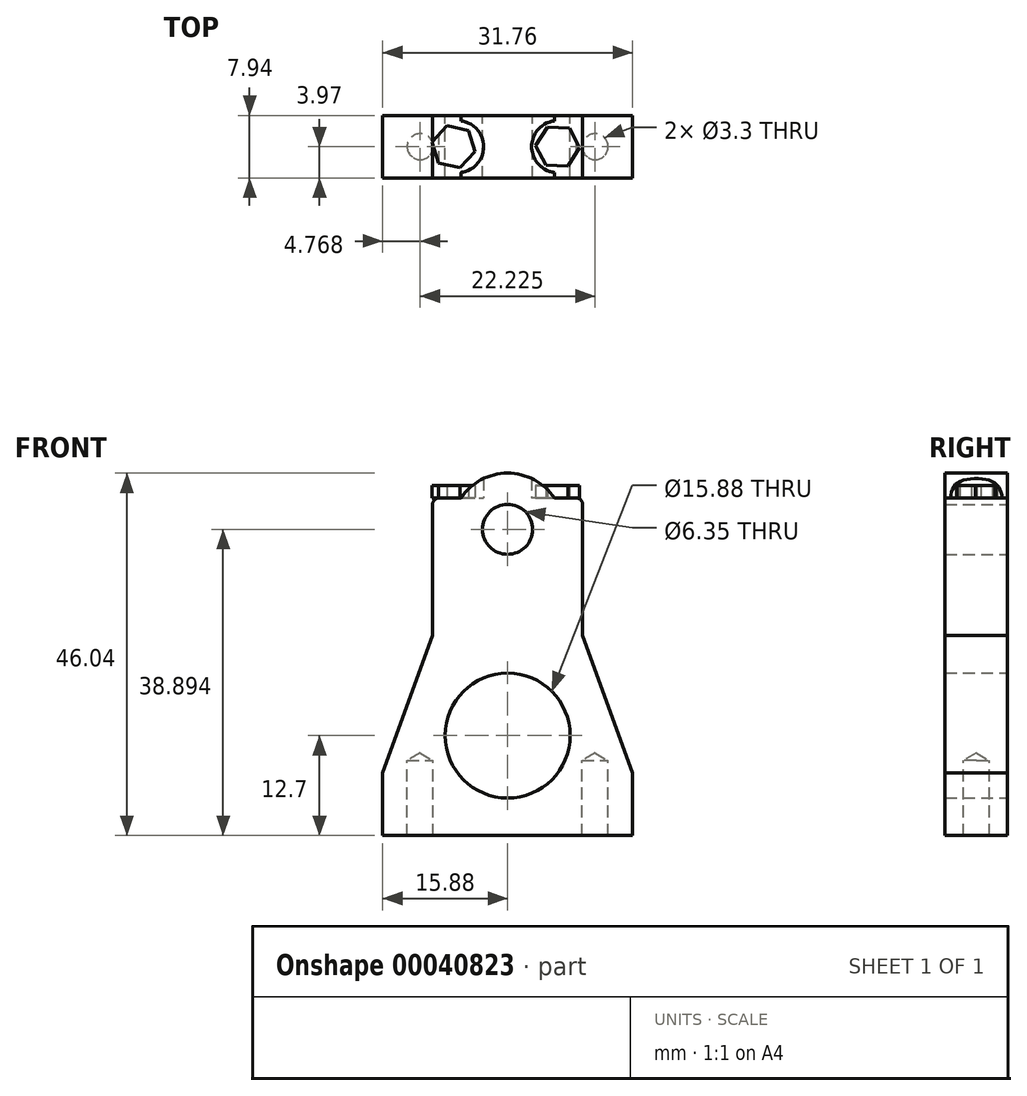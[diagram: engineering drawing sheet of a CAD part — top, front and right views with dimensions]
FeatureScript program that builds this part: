
annotation { "Feature Type Name" : "Feature", "Feature Type Description" : "" }
export const myFeature = defineFeature(function(context is Context, id is Id, definition is map)
    precondition{}
    {
        {
            var Q0;
            Q0=qCreatedBy(makeId("Front.planeOp"),FACE);
            var sketch = newSketch(context, id + "F0", { "sketchPlane" : qUnion([Q0])});
            skLineSegment(sketch, "E0.bottom", {"start": v(-15.88, 0) * mm, "end": v(15.88, 0) * mm});
            skLineSegment(sketch, "E0.top", {"start": v(-9.53, 42.86) * mm, "end": v(-5.94, 42.86) * mm});
            skLineSegment(sketch, "E0.left", {"start": v(-15.88, 0) * mm, "end": v(-15.88, 7.94) * mm});
            skLineSegment(sketch, "E0.right", {"start": v(15.88, 0) * mm, "end": v(15.87, 7.94) * mm});
            skCircle(sketch, "E1", {"center": v(0, 12.7) * mm, "radius": 7.94 * mm});
            skLineSegment(sketch, "E2", {"start": v(-9.53, 25.4) * mm, "end": v(-15.88, 7.94) * mm});
            skLineSegment(sketch, "E3", {"start": v(-9.53, 25.4) * mm, "end": v(-9.53, 42.86) * mm});
            skLineSegment(sketch, "E4", {"start": v(9.53, 42.86) * mm, "end": v(9.53, 25.4) * mm});
            skLineSegment(sketch, "E5", {"start": v(9.53, 25.4) * mm, "end": v(15.88, 7.94) * mm});
            skLineSegment(sketch, "E6", {"start": v(-9.53, 38.9) * mm, "end": v(9.53, 38.9) * mm, "construction": true});
            skArc(sketch, "E7", {"start": v(5.94, 42.86) * mm, "mid": v(0, 46.04) * mm, "end": v(-5.94, 42.86) * mm});
            skLineSegment(sketch, "E8.trimOffspring", {"start": v(5.94, 42.86) * mm, "end": v(9.53, 42.86) * mm});
            skCircle(sketch, "E9", {"center": v(0, 38.9) * mm, "radius": 3.18 * mm});
            skSolve(sketch);
        }
        {
            var Q0;
            Q0=qSketchRegion(id+"F0",true);
            extrude(context, id + "F1", {"entities" : qUnion([Q0]), "depth" : 7.94 * mm, "symmetric" : true});
        }
        {
            var Q0;
            Q0=makeQuery(id+"F1.opExtrude","SWEPT_EDGE",EDGE,{"disambiguationData":[OSD([sQuery(id+"F0.wireOp",EDGE,"E0.top"),sQuery(id+"F0.wireOp",EDGE,"E3")])]});
            var Q1;
            Q1=makeQuery(id+"F1.opExtrude","SWEPT_EDGE",EDGE,{"disambiguationData":[OSD([sQuery(id+"F0.wireOp",EDGE,"E4"),sQuery(id+"F0.wireOp",EDGE,"E8.trimOffspring")])]});
            fillet(context, id + "F2", {"entities" : qUnion([Q0, Q1]), "radius" : 0.8 * mm, "tangentPropagation" : true, "allowEdgeOverflow" : false});
        }
        {
            var Q0;
            Q0=makeQuery(id+"F1.opExtrude","SWEPT_FACE",FACE,{"disambiguationData":[OSD([sQuery(id+"F0.wireOp",EDGE,"E0.bottom")])]});
            var sketch = newSketch(context, id + "F3", { "sketchPlane" : qUnion([Q0])});
            skPoint(sketch, "E10", {"position": v(-11.11, 0) * mm});
            skPoint(sketch, "E11", {"position": v(11.11, 0) * mm});
            skSolve(sketch);
        }
        {
            var Q0;
            Q0=sQuery(id+"F3.wireOp",VERTEX,"E10");
            var Q1;
            Q1=sQuery(id+"F3.wireOp",VERTEX,"E11");
            var Q2;
            Q2=makeQuery(id+"F1.opExtrude","SWEPT_BODY",BODY,{"disambiguationData":[OSD([sQuery(id+"F0.wireOp",EDGE,"E0.bottom"),sQuery(id+"F0.wireOp",EDGE,"E0.top"),sQuery(id+"F0.wireOp",EDGE,"E0.left"),sQuery(id+"F0.wireOp",EDGE,"E0.right"),sQuery(id+"F0.wireOp",EDGE,"E1"),sQuery(id+"F0.wireOp",EDGE,"E2"),sQuery(id+"F0.wireOp",EDGE,"E3"),sQuery(id+"F0.wireOp",EDGE,"E4"),sQuery(id+"F0.wireOp",EDGE,"E5"),sQuery(id+"F0.wireOp",EDGE,"E7"),sQuery(id+"F0.wireOp",EDGE,"E8.trimOffspring"),sQuery(id+"F0.wireOp",EDGE,"E9")])]});
            hole(context, id + "F4", {"style" : HoleStyle.SIMPLE, "holeDiameter" : 3.3 * mm, "endStyle" : HoleEndStyle.BLIND, "holeDepth" : 9.52 * mm, "locations" : qUnion([Q0, Q1]), "scope" : qUnion([Q2])});
        }
        {
            var Q0;
            Q0=makeQuery(id+"F1.opExtrude","SWEPT_FACE",FACE,{"disambiguationData":[OSD([sQuery(id+"F0.wireOp",EDGE,"E0.top")])]});
            cPlane(context, id + "F5", {"entities" : qUnion([Q0]), "cplaneType" : CPlaneType.OFFSET, "offset" : 0 * mm, "width" : 152.4 * mm, "height" : 152.4 * mm});
        }
        {
            var Q0;
            Q0=qCreatedBy(id+"F5.planeOp",FACE);
            var sketch = newSketch(context, id + "F6", { "sketchPlane" : qUnion([Q0])});
            skCircle(sketch, "E12", {"center": v(-6.35, 0) * mm, "radius": 3.3 * mm});
            skCircle(sketch, "E13", {"center": v(6.35, 0) * mm, "radius": 3.3 * mm});
            skSolve(sketch);
        }
        {
            var Q0;
            Q0=qSketchRegion(id+"F6",true);
            extrude(context, id + "F7", {"entities" : qUnion([Q0]), "operationType" : NewBodyOperationType.REMOVE, "depth" : 25.4 * mm});
        }
        {
            var Q0;
            Q0=qCreatedBy(id+"F5.planeOp",FACE);
            var sketch = newSketch(context, id + "F8", { "sketchPlane" : qUnion([Q0])});
            skCircle(sketch, "E14.cCircle", {"center": v(-6.87, 0) * mm, "radius": 2.8 * mm, "construction": true});
            skLineSegment(sketch, "E14.0", {"start": v(-7.71, 2.66) * mm, "end": v(-4.99, 2.06) * mm});
            skLineSegment(sketch, "E14.1", {"start": v(-4.99, 2.06) * mm, "end": v(-4.14, -0.6) * mm});
            skLineSegment(sketch, "E14.2", {"start": v(-4.14, -0.6) * mm, "end": v(-6.02, -2.66) * mm});
            skLineSegment(sketch, "E14.3", {"start": v(-6.02, -2.66) * mm, "end": v(-8.75, -2.06) * mm});
            skLineSegment(sketch, "E14.4", {"start": v(-8.75, -2.06) * mm, "end": v(-9.6, 0.6) * mm});
            skLineSegment(sketch, "E14.5", {"start": v(-9.6, 0.6) * mm, "end": v(-7.71, 2.66) * mm});
            skCircle(sketch, "E15.cCircle", {"center": v(6.35, 0) * mm, "radius": 2.8 * mm, "construction": true});
            skPoint(sketch, "E15.cCircle.perimeterSnap0", {"position": v(-6.35, 2.36) * mm});
            skLineSegment(sketch, "E15.0", {"start": v(7.84, 2.36) * mm, "end": v(9.14, -0.1) * mm});
            skPoint(sketch, "E15.0.startSnap0", {"position": v(-6.35, 2.36) * mm});
            skLineSegment(sketch, "E15.1", {"start": v(9.14, -0.1) * mm, "end": v(7.65, -2.47) * mm});
            skLineSegment(sketch, "E15.2", {"start": v(7.65, -2.47) * mm, "end": v(4.86, -2.36) * mm});
            skLineSegment(sketch, "E15.3", {"start": v(4.86, -2.36) * mm, "end": v(3.56, 0.1) * mm});
            skLineSegment(sketch, "E15.4", {"start": v(3.56, 0.1) * mm, "end": v(5.05, 2.47) * mm});
            skLineSegment(sketch, "E15.5", {"start": v(5.05, 2.47) * mm, "end": v(7.84, 2.36) * mm});
            skSolve(sketch);
        }
        {
            var Q0;
            Q0=qSketchRegion(id+"F8",true);
            extrude(context, id + "F9", {"entities" : qUnion([Q0]), "operationType" : NewBodyOperationType.ADD, "depth" : 1.59 * mm});
        }
    });
